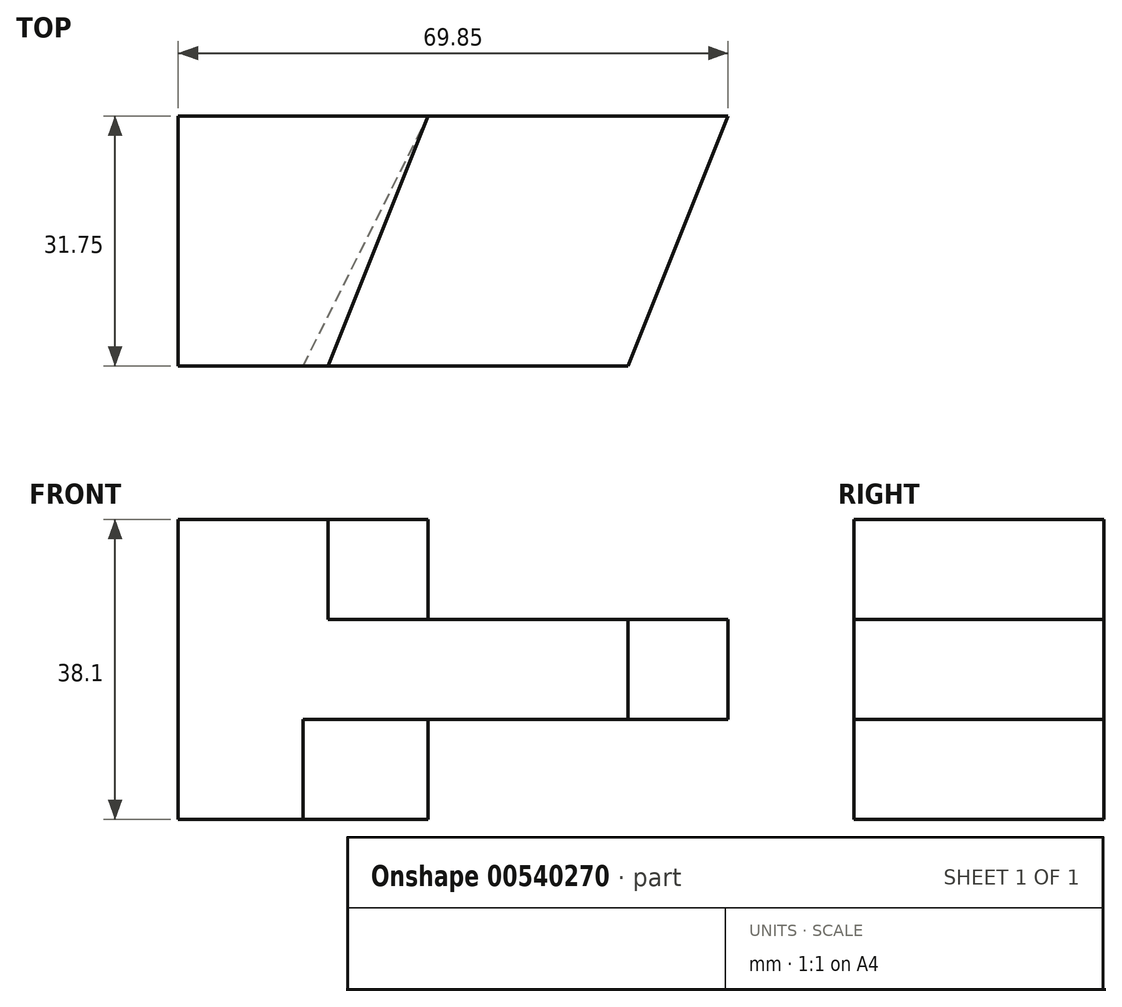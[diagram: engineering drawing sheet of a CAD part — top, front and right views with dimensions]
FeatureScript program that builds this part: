
annotation { "Feature Type Name" : "Feature", "Feature Type Description" : "" }
export const myFeature = defineFeature(function(context is Context, id is Id, definition is map)
    precondition{}
    {
        {
            var Q0;
            Q0=qCreatedBy(makeId("Front.planeOp"),FACE);
            var sketch = newSketch(context, id + "F0", { "sketchPlane" : qUnion([Q0])});
            skLineSegment(sketch, "E0", {"start": v(-78.64, 0) * mm, "end": v(-78.64, 38.1) * mm});
            skLineSegment(sketch, "E1", {"start": v(-78.64, 38.1) * mm, "end": v(-46.9, 38.1) * mm});
            skLineSegment(sketch, "E2", {"start": v(-46.9, 38.1) * mm, "end": v(-46.9, 25.4) * mm});
            skLineSegment(sketch, "E3", {"start": v(-46.9, 25.4) * mm, "end": v(-8.8, 25.4) * mm});
            skLineSegment(sketch, "E4", {"start": v(-8.8, 25.4) * mm, "end": v(-8.8, 12.7) * mm});
            skLineSegment(sketch, "E5", {"start": v(-8.8, 12.7) * mm, "end": v(-46.9, 12.7) * mm});
            skLineSegment(sketch, "E6", {"start": v(-46.9, 12.7) * mm, "end": v(-46.9, 0) * mm});
            skLineSegment(sketch, "E7", {"start": v(-46.9, 0) * mm, "end": v(-78.64, 0) * mm});
            skSolve(sketch);
        }
        {
            var Q0;
            Q0=makeQuery(id+"F0.imprint","IMPRINT",FACE,{"disambiguationData":[TD([[makeQuery(id+"F0.imprint","IMPRINT",EDGE,{"derivedFrom":sQuery(id+"F0.wireOp",EDGE,"E0")}),-1.0]])]});
            extrude(context, id + "F1", {"entities" : qUnion([Q0]), "depth" : 31.75 * mm, "offsetDistance" : 25.4 * mm});
        }
        {
            var Q0;
            Q0=makeQuery(id+"F1.opExtrude","SWEPT_FACE",FACE,{"disambiguationData":[OSD([sQuery(id+"F0.wireOp",EDGE,"E7")])]});
            var sketch = newSketch(context, id + "F2", { "sketchPlane" : qUnion([Q0])});
            skLineSegment(sketch, "E8", {"start": v(-62.77, 31.75) * mm, "end": v(-46.9, 0) * mm});
            skSolve(sketch);
        }
        {
            var Q0;
            {var subQ0=sQuery(id+"F2.wireOp",EDGE,"E8");Q0=makeQuery(id+"F2.imprint","IMPRINT",FACE,{"disambiguationData":[TD([[makeQuery(id+"F2.imprint","IMPRINT",EDGE,{"derivedFrom":subQ0}),1.0]])]});}
            extrude(context, id + "F3", {"entities" : qUnion([Q0]), "operationType" : NewBodyOperationType.REMOVE, "oppositeDirection" : true, "depth" : 12.7 * mm, "offsetDistance" : 25.4 * mm});
        }
        {
            var Q0;
            Q0=makeQuery(id+"F1.opExtrude","SWEPT_FACE",FACE,{"disambiguationData":[OSD([sQuery(id+"F0.wireOp",EDGE,"E1")])]});
            var sketch = newSketch(context, id + "F4", { "sketchPlane" : qUnion([Q0])});
            skLineSegment(sketch, "E9", {"start": v(-59.6, -31.75) * mm, "end": v(-46.9, 0) * mm});
            skSolve(sketch);
        }
        {
            var Q0;
            Q0 = qSketchRegion(id + "F4", true);
            var Q1;
            {var subQ0=sQuery(id+"F4.wireOp",EDGE,"E9");Q1=makeQuery(id+"F4.imprint","IMPRINT",FACE,{"disambiguationData":[TD([[makeQuery(id+"F4.imprint","IMPRINT",EDGE,{"derivedFrom":subQ0}),-1.0]])]});}
            extrude(context, id + "F5", {"entities" : qUnion([Q0, Q1]), "operationType" : NewBodyOperationType.REMOVE, "oppositeDirection" : true, "depth" : 12.7 * mm, "offsetDistance" : 25.4 * mm});
        }
        {
            var Q0;
            Q0=makeQuery(id+"F3.boolean.opBoolean","MERGE",FACE,{"derivedFrom":[makeQuery(id+"F1.opExtrude","SWEPT_FACE",FACE,{"disambiguationData":[OSD([sQuery(id+"F0.wireOp",EDGE,"E5")])]}),makeQuery(id+"F3.opExtrude","CAP_FACE",FACE,{"disambiguationData":[OSD([sQuery(id+"F0.wireOp",EDGE,"E6"),sQuery(id+"F0.wireOp",EDGE,"E7"),sQuery(id+"F2.wireOp",EDGE,"E8")])],"isStart":false})]});
            var sketch = newSketch(context, id + "F6", { "sketchPlane" : qUnion([Q0])});
            skLineSegment(sketch, "E10", {"start": v(-21.5, 31.75) * mm, "end": v(-8.8, 0) * mm});
            skSolve(sketch);
        }
        {
            var Q0;
            Q0 = qSketchRegion(id + "F6", true);
            var Q1;
            {var subQ0=sQuery(id+"F6.wireOp",EDGE,"E10");Q1=makeQuery(id+"F6.imprint","IMPRINT",FACE,{"disambiguationData":[TD([[makeQuery(id+"F6.imprint","IMPRINT",EDGE,{"derivedFrom":subQ0}),1.0]])]});}
            extrude(context, id + "F7", {"entities" : qUnion([Q0, Q1]), "operationType" : NewBodyOperationType.REMOVE, "oppositeDirection" : true, "depth" : 12.7 * mm, "offsetDistance" : 25.4 * mm});
        }
    });
